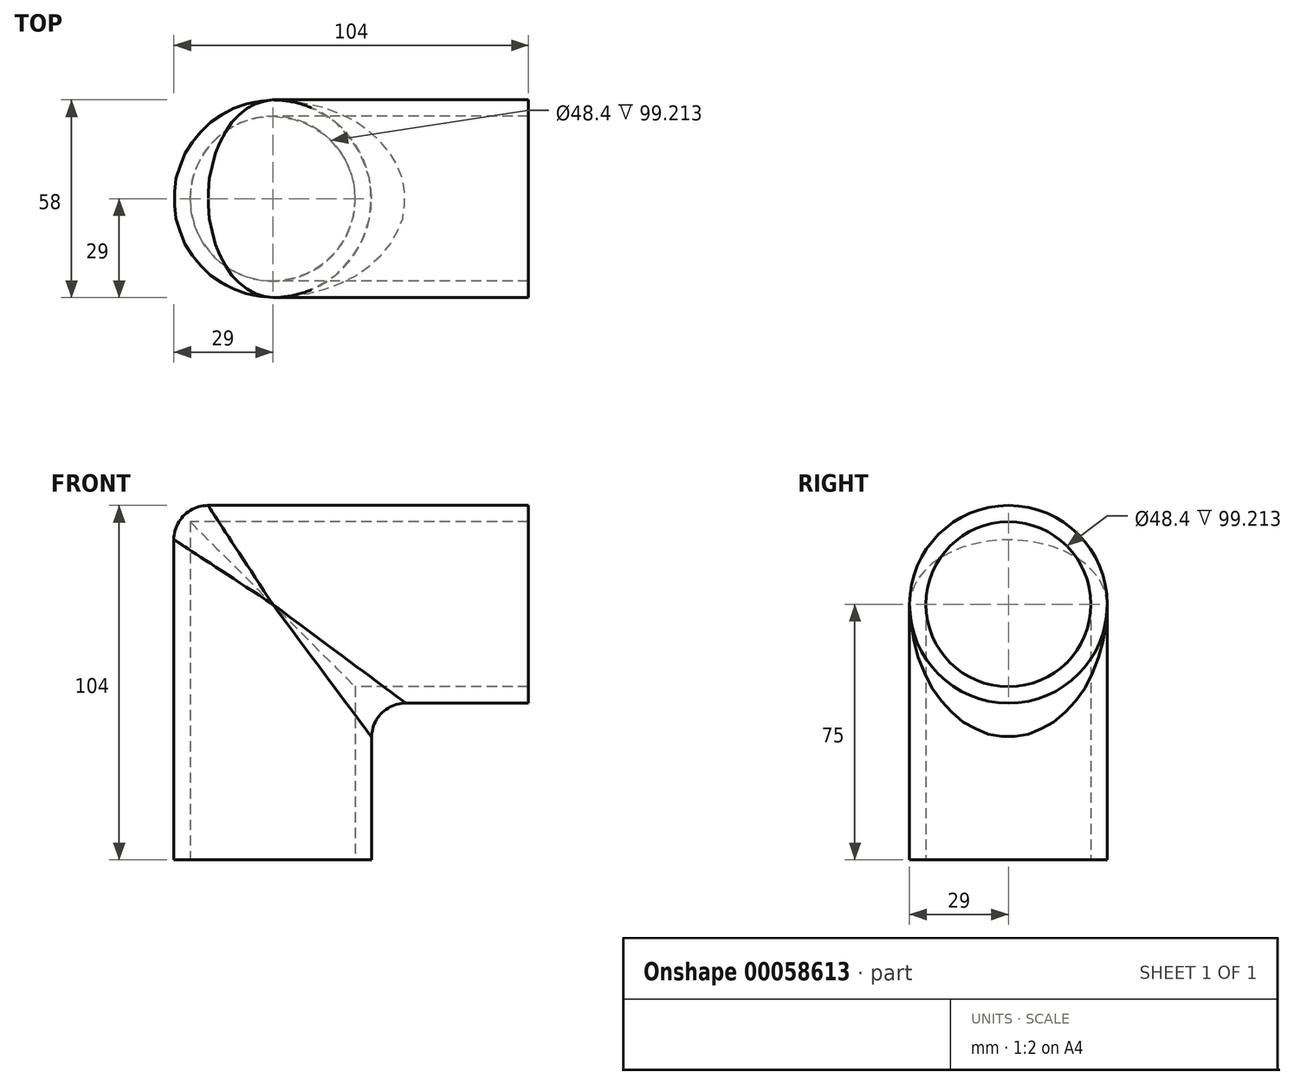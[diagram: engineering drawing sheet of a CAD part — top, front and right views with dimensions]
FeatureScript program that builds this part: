
annotation { "Feature Type Name" : "Feature", "Feature Type Description" : "" }
export const myFeature = defineFeature(function(context is Context, id is Id, definition is map)
    precondition{}
    {
        {
            var Q0;
            Q0=qCreatedBy(makeId("Right.planeOp"),FACE);
            var sketch = newSketch(context, id + "F0", { "sketchPlane" : qUnion([Q0])});
            skCircle(sketch, "E0", {"center": v(0, 0) * mm, "radius": 29 * mm});
            skCircle(sketch, "E1", {"center": v(0, 0) * mm, "radius": 24.2 * mm});
            skSolve(sketch);
        }
        {
            var Q0;
            Q0=qCreatedBy(makeId("Front.planeOp"),FACE);
            var sketch = newSketch(context, id + "F1", { "sketchPlane" : qUnion([Q0])});
            skLineSegment(sketch, "E2", {"start": v(0, 0) * mm, "end": v(-75, 0) * mm});
            skLineSegment(sketch, "E3", {"start": v(-75, 0) * mm, "end": v(-75, -75) * mm});
            skSolve(sketch);
        }
        {
            var Q0;
            Q0=makeQuery(id+"F0.imprint","IMPRINT",FACE,{"disambiguationData":[TD([[makeQuery(id+"F0.imprint","IMPRINT",EDGE,{"derivedFrom":sQuery(id+"F0.wireOp",EDGE,"E0")}),1.0]])]});
            var Q1;
            Q1=sQuery(id+"F1.wireOp",EDGE,"E2");
            var Q2;
            Q2=sQuery(id+"F1.wireOp",EDGE,"E3");
            sweep(context, id + "F2", {"profiles" : qUnion([Q0]), "path" : qUnion([Q1, Q2])});
        }
        {
            var Q0;
            Q0=makeQuery(id+"F2.opSweep","MID_CAP_EDGE",EDGE,{"disambiguationData":[OSD([sQuery(id+"F0.wireOp",EDGE,"E0"),sQuery(id+"F1.wireOp",VERTEX,"E3.start")])],"capPos":1.0});
            fillet(context, id + "F3", {"entities" : qUnion([Q0]), "radius" : 10 * mm, "tangentPropagation" : true, "allowEdgeOverflow" : false});
        }
    });
